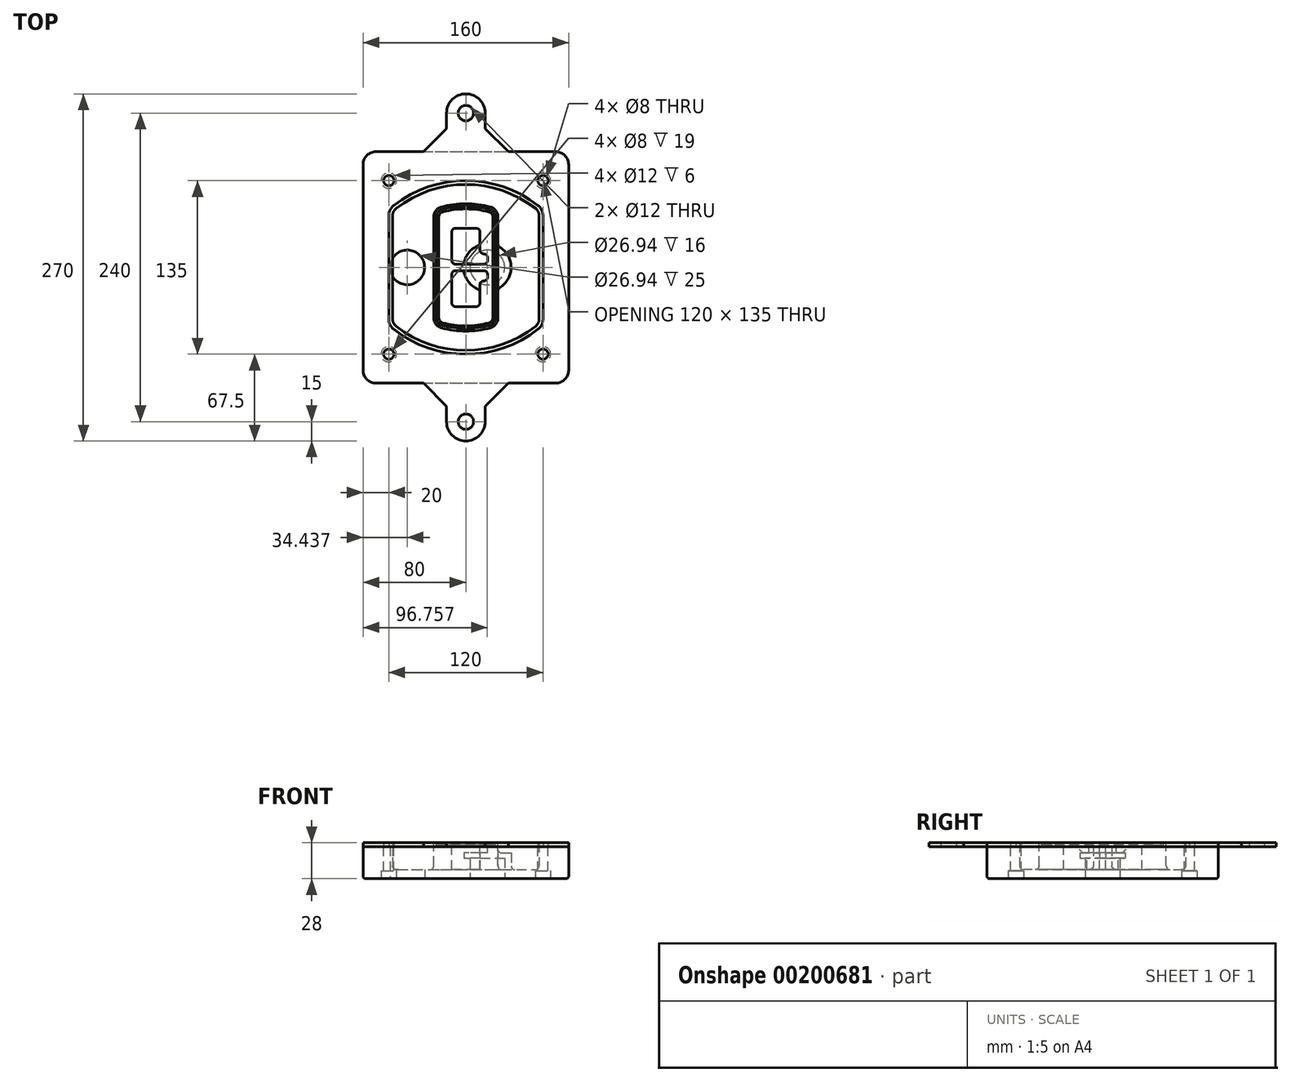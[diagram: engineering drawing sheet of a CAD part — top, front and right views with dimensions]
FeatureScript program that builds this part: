
annotation { "Feature Type Name" : "Feature", "Feature Type Description" : "" }
export const myFeature = defineFeature(function(context is Context, id is Id, definition is map)
    precondition{}
    {
        {
            var Q0;
            Q0=qCreatedBy(makeId("Top.planeOp"),FACE);
            var sketch = newSketch(context, id + "F0", { "sketchPlane" : qUnion([Q0])});
            skPoint(sketch, "E0.rect.middle", {"position": v(0, 0) * mm});
            skLineSegment(sketch, "E1.bottom", {"start": v(-70, -90) * mm, "end": v(70, -90) * mm});
            skLineSegment(sketch, "E1.top", {"start": v(-70, 90) * mm, "end": v(70, 90) * mm});
            skLineSegment(sketch, "E1.left", {"start": v(-80, -80) * mm, "end": v(-80, 80) * mm});
            skLineSegment(sketch, "E1.right", {"start": v(80, -80) * mm, "end": v(80, 80) * mm});
            skLineSegment(sketch, "E2", {"start": v(-80, 90) * mm, "end": v(80, -90) * mm, "construction": true});
            skLineSegment(sketch, "E3", {"start": v(80, 90) * mm, "end": v(-80, -90) * mm, "construction": true});
            skCircle(sketch, "E4", {"center": v(-60, 67.5) * mm, "radius": 4 * mm});
            skCircle(sketch, "E5", {"center": v(60, 67.5) * mm, "radius": 4 * mm});
            skCircle(sketch, "E6", {"center": v(60, -67.5) * mm, "radius": 4 * mm});
            skCircle(sketch, "E7", {"center": v(-60, -67.5) * mm, "radius": 4 * mm});
            skLineSegment(sketch, "E8", {"start": v(-60, 67.5) * mm, "end": v(60, 67.5) * mm, "construction": true});
            skLineSegment(sketch, "E9", {"start": v(60, 67.5) * mm, "end": v(60, -67.5) * mm, "construction": true});
            skLineSegment(sketch, "E10", {"start": v(60, -67.5) * mm, "end": v(-60, -67.5) * mm, "construction": true});
            skLineSegment(sketch, "E11", {"start": v(-60, -67.5) * mm, "end": v(-60, 67.5) * mm, "construction": true});
            skLineSegment(sketch, "E12", {"start": v(-60, 40.3) * mm, "end": v(-60, -40.3) * mm});
            skLineSegment(sketch, "E13", {"start": v(60, 40.3) * mm, "end": v(60, -40.3) * mm});
            skArc(sketch, "E14", {"start": v(56.15, 48.18) * mm, "mid": v(0, 67.5) * mm, "end": v(-56.15, 48.18) * mm});
            skArc(sketch, "E15", {"start": v(-56.15, -48.18) * mm, "mid": v(0, -67.5) * mm, "end": v(56.15, -48.18) * mm});
            skLineSegment(sketch, "E16", {"start": v(-60, 0) * mm, "end": v(60, 0) * mm, "construction": true});
            skPoint(sketch, "E17.visualSharp", {"position": v(-60, -45) * mm});
            skArc(sketch, "E17.filletArc", {"start": v(-60, -40.3) * mm, "mid": v(-58.99, -44.68) * mm, "end": v(-56.15, -48.18) * mm});
            skPoint(sketch, "E18.visualSharp", {"position": v(-60, 45) * mm});
            skArc(sketch, "E18.filletArc", {"start": v(-56.15, 48.18) * mm, "mid": v(-58.99, 44.68) * mm, "end": v(-60, 40.3) * mm});
            skPoint(sketch, "E19.visualSharp", {"position": v(60, 45) * mm});
            skArc(sketch, "E19.filletArc", {"start": v(60, 40.3) * mm, "mid": v(58.99, 44.68) * mm, "end": v(56.15, 48.18) * mm});
            skPoint(sketch, "E20.visualSharp", {"position": v(60, -45) * mm});
            skArc(sketch, "E20.filletArc", {"start": v(56.15, -48.18) * mm, "mid": v(58.99, -44.68) * mm, "end": v(60, -40.3) * mm});
            skPoint(sketch, "E21.visualSharp", {"position": v(-80, 90) * mm});
            skArc(sketch, "E21.filletArc", {"start": v(-70, 90) * mm, "mid": v(-77.07, 87.07) * mm, "end": v(-80, 80) * mm});
            skPoint(sketch, "E22.visualSharp", {"position": v(80, 90) * mm});
            skArc(sketch, "E22.filletArc", {"start": v(80, 80) * mm, "mid": v(77.07, 87.07) * mm, "end": v(70, 90) * mm});
            skPoint(sketch, "E23.visualSharp", {"position": v(80, -90) * mm});
            skArc(sketch, "E23.filletArc", {"start": v(70, -90) * mm, "mid": v(77.07, -87.07) * mm, "end": v(80, -80) * mm});
            skPoint(sketch, "E24.visualSharp", {"position": v(-80, -90) * mm});
            skArc(sketch, "E24.filletArc", {"start": v(-80, -80) * mm, "mid": v(-77.07, -87.07) * mm, "end": v(-70, -90) * mm});
            skArc(sketch, "E25.0", {"start": v(57, 40.3) * mm, "mid": v(56.3, 43.36) * mm, "end": v(54.3, 45.81) * mm});
            skLineSegment(sketch, "E25.1", {"start": v(57, 40.3) * mm, "end": v(57, -40.3) * mm});
            skArc(sketch, "E25.2", {"start": v(54.3, -45.81) * mm, "mid": v(56.3, -43.36) * mm, "end": v(57, -40.3) * mm});
            skArc(sketch, "E25.3", {"start": v(-54.3, -45.81) * mm, "mid": v(0, -64.5) * mm, "end": v(54.3, -45.81) * mm});
            skArc(sketch, "E25.4", {"start": v(-57, -40.3) * mm, "mid": v(-56.3, -43.36) * mm, "end": v(-54.3, -45.81) * mm});
            skArc(sketch, "E25.5", {"start": v(54.3, 45.81) * mm, "mid": v(0, 64.5) * mm, "end": v(-54.3, 45.81) * mm});
            skLineSegment(sketch, "E25.6", {"start": v(-57, 40.3) * mm, "end": v(-57, -40.3) * mm});
            skArc(sketch, "E25.7", {"start": v(-54.3, 45.81) * mm, "mid": v(-56.3, 43.36) * mm, "end": v(-57, 40.3) * mm});
            skArc(sketch, "E26.0", {"start": v(-58.62, 51.33) * mm, "mid": v(-62.58, 46.43) * mm, "end": v(-64, 40.3) * mm});
            skArc(sketch, "E26.1", {"start": v(58.62, 51.33) * mm, "mid": v(0, 71.5) * mm, "end": v(-58.62, 51.33) * mm});
            skArc(sketch, "E26.2", {"start": v(64, 40.3) * mm, "mid": v(62.58, 46.43) * mm, "end": v(58.62, 51.33) * mm});
            skLineSegment(sketch, "E26.3", {"start": v(64, 40.3) * mm, "end": v(64, -40.3) * mm});
            skArc(sketch, "E26.4", {"start": v(58.62, -51.33) * mm, "mid": v(62.58, -46.43) * mm, "end": v(64, -40.3) * mm});
            skLineSegment(sketch, "E26.5", {"start": v(-64, 40.3) * mm, "end": v(-64, -40.3) * mm});
            skArc(sketch, "E26.6", {"start": v(-58.62, -51.33) * mm, "mid": v(0, -71.5) * mm, "end": v(58.62, -51.33) * mm});
            skArc(sketch, "E26.7", {"start": v(-64, -40.3) * mm, "mid": v(-62.58, -46.43) * mm, "end": v(-58.62, -51.33) * mm});
            skSolve(sketch);
        }
        {
            var Q0;
            Q0=makeQuery(id+"F0.imprint","IMPRINT",FACE,{"disambiguationData":[TD([[makeQuery(id+"F0.imprint","IMPRINT",EDGE,{"derivedFrom":sQuery(id+"F0.wireOp",EDGE,"E1.bottom")}),1.0]])]});
            var Q1;
            Q1=makeQuery(id+"F0.imprint","IMPRINT",FACE,{"disambiguationData":[TD([[makeQuery(id+"F0.imprint","IMPRINT",EDGE,{"derivedFrom":sQuery(id+"F0.wireOp",EDGE,"E12")}),1.0]])]});
            var Q2;
            Q2=makeQuery(id+"F0.imprint","IMPRINT",FACE,{"disambiguationData":[TD([[makeQuery(id+"F0.imprint","IMPRINT",EDGE,{"derivedFrom":sQuery(id+"F0.wireOp",EDGE,"E25.0")}),1.0]])]});
            var Q3;
            Q3=makeQuery(id+"F0.imprint","IMPRINT",FACE,{"disambiguationData":[TD([[makeQuery(id+"F0.imprint","IMPRINT",EDGE,{"derivedFrom":sQuery(id+"F0.wireOp",EDGE,"E12")}),-1.0]])]});
            extrude(context, id + "F1", {"entities" : qUnion([Q0, Q1, Q2, Q3]), "oppositeDirection" : true, "depth" : 25 * mm});
        }
        {
            var Q0;
            Q0=makeQuery(id+"F0.imprint","IMPRINT",FACE,{"disambiguationData":[TD([[makeQuery(id+"F0.imprint","IMPRINT",EDGE,{"derivedFrom":sQuery(id+"F0.wireOp",EDGE,"E12")}),1.0]])]});
            extrude(context, id + "F2", {"entities" : qUnion([Q0]), "operationType" : NewBodyOperationType.ADD, "depth" : 3 * mm});
        }
        {
            var Q0;
            Q0=makeQuery(id+"F0.imprint","IMPRINT",FACE,{"disambiguationData":[TD([[makeQuery(id+"F0.imprint","IMPRINT",EDGE,{"derivedFrom":sQuery(id+"F0.wireOp",EDGE,"E25.0")}),1.0]])]});
            extrude(context, id + "F3", {"entities" : qUnion([Q0]), "operationType" : NewBodyOperationType.REMOVE, "oppositeDirection" : true, "depth" : 18 * mm});
        }
        {
            var Q0;
            Q0=makeQuery(id+"F2.opExtrude","CAP_FACE",FACE,{"disambiguationData":[OSD([sQuery(id+"F0.wireOp",EDGE,"E12"),sQuery(id+"F0.wireOp",EDGE,"E13"),sQuery(id+"F0.wireOp",EDGE,"E14"),sQuery(id+"F0.wireOp",EDGE,"E15"),sQuery(id+"F0.wireOp",EDGE,"E17.filletArc"),sQuery(id+"F0.wireOp",EDGE,"E18.filletArc"),sQuery(id+"F0.wireOp",EDGE,"E19.filletArc"),sQuery(id+"F0.wireOp",EDGE,"E20.filletArc"),sQuery(id+"F0.wireOp",EDGE,"E25.0"),sQuery(id+"F0.wireOp",EDGE,"E25.1"),sQuery(id+"F0.wireOp",EDGE,"E25.2"),sQuery(id+"F0.wireOp",EDGE,"E25.3"),sQuery(id+"F0.wireOp",EDGE,"E25.4"),sQuery(id+"F0.wireOp",EDGE,"E25.5"),sQuery(id+"F0.wireOp",EDGE,"E25.6"),sQuery(id+"F0.wireOp",EDGE,"E25.7")])],"isStart":false});
            var sketch = newSketch(context, id + "F4", { "sketchPlane" : qUnion([Q0])});
            skArc(sketch, "E27.0", {"start": v(-19.08, -46.97) * mm, "mid": v(0, -49.5) * mm, "end": v(19.08, -46.97) * mm});
            skArc(sketch, "E28.0", {"start": v(19.08, 46.97) * mm, "mid": v(0, 49.5) * mm, "end": v(-19.08, 46.97) * mm});
            skLineSegment(sketch, "E29", {"start": v(-25, 39.25) * mm, "end": v(-25, -39.25) * mm});
            skLineSegment(sketch, "E30", {"start": v(25, 39.25) * mm, "end": v(25, -39.25) * mm});
            skLineSegment(sketch, "E31", {"start": v(-25, 45.1) * mm, "end": v(25, 45.1) * mm, "construction": true});
            skLineSegment(sketch, "E32", {"start": v(-25, -45.1) * mm, "end": v(25, -45.1) * mm, "construction": true});
            skPoint(sketch, "E33.visualSharp", {"position": v(-25, 45.1) * mm});
            skArc(sketch, "E33.filletArc", {"start": v(-19.08, 46.97) * mm, "mid": v(-23.35, 44.11) * mm, "end": v(-25, 39.25) * mm});
            skPoint(sketch, "E34.visualSharp", {"position": v(25, 45.1) * mm});
            skArc(sketch, "E34.filletArc", {"start": v(25, 39.25) * mm, "mid": v(23.35, 44.11) * mm, "end": v(19.08, 46.97) * mm});
            skPoint(sketch, "E35.visualSharp", {"position": v(25, -45.1) * mm});
            skArc(sketch, "E35.filletArc", {"start": v(19.08, -46.97) * mm, "mid": v(23.35, -44.11) * mm, "end": v(25, -39.25) * mm});
            skPoint(sketch, "E36.visualSharp", {"position": v(-25, -45.1) * mm});
            skArc(sketch, "E36.filletArc", {"start": v(-25, -39.25) * mm, "mid": v(-23.35, -44.11) * mm, "end": v(-19.08, -46.97) * mm});
            skArc(sketch, "E37.0", {"start": v(54.3, 45.81) * mm, "mid": v(0, 64.5) * mm, "end": v(-54.3, 45.81) * mm});
            skArc(sketch, "E37.1", {"start": v(-54.3, 45.81) * mm, "mid": v(-56.3, 43.36) * mm, "end": v(-57, 40.3) * mm});
            skLineSegment(sketch, "E37.2", {"start": v(-57, 40.3) * mm, "end": v(-57, -40.3) * mm});
            skArc(sketch, "E37.3", {"start": v(-57, -40.3) * mm, "mid": v(-56.3, -43.36) * mm, "end": v(-54.3, -45.81) * mm});
            skArc(sketch, "E37.4", {"start": v(-54.3, -45.81) * mm, "mid": v(0, -64.5) * mm, "end": v(54.3, -45.81) * mm});
            skArc(sketch, "E37.5", {"start": v(54.3, -45.81) * mm, "mid": v(56.3, -43.36) * mm, "end": v(57, -40.3) * mm});
            skLineSegment(sketch, "E37.6", {"start": v(57, 40.3) * mm, "end": v(57, -40.3) * mm});
            skArc(sketch, "E37.7", {"start": v(57, 40.3) * mm, "mid": v(56.3, 43.36) * mm, "end": v(54.3, 45.81) * mm});
            skLineSegment(sketch, "E38.0", {"start": v(23, 39.25) * mm, "end": v(23, -39.25) * mm});
            skArc(sketch, "E38.1", {"start": v(18.56, -45.04) * mm, "mid": v(21.76, -42.9) * mm, "end": v(23, -39.25) * mm});
            skArc(sketch, "E38.2", {"start": v(-18.56, -45.04) * mm, "mid": v(0, -47.5) * mm, "end": v(18.56, -45.04) * mm});
            skArc(sketch, "E38.3", {"start": v(-23, -39.25) * mm, "mid": v(-21.76, -42.9) * mm, "end": v(-18.56, -45.04) * mm});
            skLineSegment(sketch, "E38.4", {"start": v(-23, 39.25) * mm, "end": v(-23, -39.25) * mm});
            skArc(sketch, "E38.5", {"start": v(23, 39.25) * mm, "mid": v(21.76, 42.9) * mm, "end": v(18.56, 45.04) * mm});
            skArc(sketch, "E38.6", {"start": v(-18.56, 45.04) * mm, "mid": v(-21.76, 42.9) * mm, "end": v(-23, 39.25) * mm});
            skArc(sketch, "E38.7", {"start": v(18.56, 45.04) * mm, "mid": v(0, 47.5) * mm, "end": v(-18.56, 45.04) * mm});
            skArc(sketch, "E39.0", {"start": v(21, 39.25) * mm, "mid": v(20.18, 41.68) * mm, "end": v(18.04, 43.1) * mm});
            skLineSegment(sketch, "E39.1", {"start": v(21, 39.25) * mm, "end": v(21, -39.25) * mm});
            skArc(sketch, "E39.2", {"start": v(18.04, -43.1) * mm, "mid": v(20.18, -41.68) * mm, "end": v(21, -39.25) * mm});
            skArc(sketch, "E39.3", {"start": v(-18.04, -43.1) * mm, "mid": v(0, -45.5) * mm, "end": v(18.04, -43.1) * mm});
            skArc(sketch, "E39.4", {"start": v(-21, -39.25) * mm, "mid": v(-20.18, -41.68) * mm, "end": v(-18.04, -43.1) * mm});
            skArc(sketch, "E39.5", {"start": v(18.04, 43.1) * mm, "mid": v(0, 45.5) * mm, "end": v(-18.04, 43.1) * mm});
            skLineSegment(sketch, "E39.6", {"start": v(-21, 39.25) * mm, "end": v(-21, -39.25) * mm});
            skArc(sketch, "E39.7", {"start": v(-18.04, 43.1) * mm, "mid": v(-20.18, 41.68) * mm, "end": v(-21, 39.25) * mm});
            skLineSegment(sketch, "E40", {"start": v(-25, 0) * mm, "end": v(25, 0) * mm, "construction": true});
            skLineSegment(sketch, "E41", {"start": v(-11, 5.5) * mm, "end": v(-11, 27.5) * mm});
            skLineSegment(sketch, "E42", {"start": v(-8, 30.5) * mm, "end": v(8, 30.5) * mm});
            skLineSegment(sketch, "E43", {"start": v(11, 27.5) * mm, "end": v(11, 13.5) * mm});
            skLineSegment(sketch, "E44", {"start": v(14, 10.5) * mm, "end": v(14, 10.5) * mm});
            skLineSegment(sketch, "E45", {"start": v(17, 7.5) * mm, "end": v(17, 5.5) * mm});
            skLineSegment(sketch, "E46", {"start": v(14, 2.5) * mm, "end": v(-8, 2.5) * mm});
            skPoint(sketch, "E47.visualSharp", {"position": v(-11, 30.5) * mm});
            skArc(sketch, "E47.filletArc", {"start": v(-8, 30.5) * mm, "mid": v(-10.12, 29.62) * mm, "end": v(-11, 27.5) * mm});
            skPoint(sketch, "E48.visualSharp", {"position": v(11, 30.5) * mm});
            skArc(sketch, "E48.filletArc", {"start": v(11, 27.5) * mm, "mid": v(10.12, 29.62) * mm, "end": v(8, 30.5) * mm});
            skPoint(sketch, "E49.visualSharp", {"position": v(11, 10.5) * mm});
            skArc(sketch, "E49.filletArc", {"start": v(11, 13.5) * mm, "mid": v(11.88, 11.38) * mm, "end": v(14, 10.5) * mm});
            skPoint(sketch, "E50.visualSharp", {"position": v(17, 10.5) * mm});
            skArc(sketch, "E50.filletArc", {"start": v(17, 7.5) * mm, "mid": v(16.12, 9.62) * mm, "end": v(14, 10.5) * mm});
            skPoint(sketch, "E51.visualSharp", {"position": v(17, 2.5) * mm});
            skArc(sketch, "E51.filletArc", {"start": v(14, 2.5) * mm, "mid": v(16.12, 3.38) * mm, "end": v(17, 5.5) * mm});
            skPoint(sketch, "E52.visualSharp", {"position": v(-11, 2.5) * mm});
            skArc(sketch, "E52.filletArc", {"start": v(-11, 5.5) * mm, "mid": v(-10.12, 3.38) * mm, "end": v(-8, 2.5) * mm});
            skLineSegment(sketch, "E53.0.MirrorCS", {"start": v(14, -2.5) * mm, "end": v(-8, -2.5) * mm});
            skArc(sketch, "E54.0.MirrorCS", {"start": v(-11, -5.5) * mm, "mid": v(-10.12, -3.38) * mm, "end": v(-8, -2.5) * mm});
            skLineSegment(sketch, "E55.0.MirrorCS", {"start": v(-11, -5.5) * mm, "end": v(-11, -27.5) * mm});
            skArc(sketch, "E56.0.MirrorCS", {"start": v(-8, -30.5) * mm, "mid": v(-10.12, -29.62) * mm, "end": v(-11, -27.5) * mm});
            skLineSegment(sketch, "E57.0.MirrorCS", {"start": v(-8, -30.5) * mm, "end": v(8, -30.5) * mm});
            skArc(sketch, "E58.0.MirrorCS", {"start": v(11, -27.5) * mm, "mid": v(10.12, -29.62) * mm, "end": v(8, -30.5) * mm});
            skLineSegment(sketch, "E59.0.MirrorCS", {"start": v(11, -27.5) * mm, "end": v(11, -13.5) * mm});
            skArc(sketch, "E60.0.MirrorCS", {"start": v(11, -13.5) * mm, "mid": v(11.88, -11.38) * mm, "end": v(14, -10.5) * mm});
            skArc(sketch, "E61.0.MirrorCS", {"start": v(17, -7.5) * mm, "mid": v(16.12, -9.62) * mm, "end": v(14, -10.5) * mm});
            skLineSegment(sketch, "E62.0.MirrorCS", {"start": v(17, -7.5) * mm, "end": v(17, -5.5) * mm});
            skArc(sketch, "E63.0.MirrorCS", {"start": v(14, -2.5) * mm, "mid": v(16.12, -3.38) * mm, "end": v(17, -5.5) * mm});
            skSolve(sketch);
        }
        {
            var Q0;
            Q0=makeQuery(id+"F4.imprint","IMPRINT",FACE,{"disambiguationData":[TD([[makeQuery(id+"F4.imprint","IMPRINT",EDGE,{"derivedFrom":sQuery(id+"F4.wireOp",EDGE,"E27.0")}),1.0]])]});
            var Q1;
            Q1=makeQuery(id+"F4.imprint","IMPRINT",FACE,{"disambiguationData":[TD([[makeQuery(id+"F4.imprint","IMPRINT",EDGE,{"derivedFrom":sQuery(id+"F4.wireOp",EDGE,"E38.0")}),-1.0]])]});
            var Q2;
            Q2=makeQuery(id+"F4.imprint","IMPRINT",FACE,{"disambiguationData":[TD([[makeQuery(id+"F4.imprint","IMPRINT",EDGE,{"derivedFrom":sQuery(id+"F4.wireOp",EDGE,"E39.0")}),1.0]])]});
            extrude(context, id + "F5", {"entities" : qUnion([Q0, Q1, Q2]), "operationType" : NewBodyOperationType.ADD, "endBound" : BoundingType.UP_TO_NEXT, "oppositeDirection" : true, "depth" : 25 * mm});
        }
        {
            var Q0;
            Q0=makeQuery(id+"F4.imprint","IMPRINT",FACE,{"disambiguationData":[TD([[makeQuery(id+"F4.imprint","IMPRINT",EDGE,{"derivedFrom":sQuery(id+"F4.wireOp",EDGE,"E38.0")}),-1.0]])]});
            extrude(context, id + "F6", {"entities" : qUnion([Q0]), "operationType" : NewBodyOperationType.REMOVE, "oppositeDirection" : true, "depth" : 2 * mm});
        }
        {
            var Q0;
            Q0=makeQuery(id+"F1.opExtrude","CAP_FACE",FACE,{"disambiguationData":[OSD([sQuery(id+"F0.wireOp",EDGE,"E1.bottom"),sQuery(id+"F0.wireOp",EDGE,"E1.top"),sQuery(id+"F0.wireOp",EDGE,"E1.left"),sQuery(id+"F0.wireOp",EDGE,"E1.right"),sQuery(id+"F0.wireOp",EDGE,"E4"),sQuery(id+"F0.wireOp",EDGE,"E5"),sQuery(id+"F0.wireOp",EDGE,"E6"),sQuery(id+"F0.wireOp",EDGE,"E7"),sQuery(id+"F0.wireOp",EDGE,"E21.filletArc"),sQuery(id+"F0.wireOp",EDGE,"E22.filletArc"),sQuery(id+"F0.wireOp",EDGE,"E23.filletArc"),sQuery(id+"F0.wireOp",EDGE,"E24.filletArc")])],"isStart":false});
            var sketch = newSketch(context, id + "F7", { "sketchPlane" : qUnion([Q0])});
            skCircle(sketch, "E64", {"center": v(16.76, 0) * mm, "radius": 13.47 * mm});
            skCircle(sketch, "E65", {"center": v(-45.56, 0) * mm, "radius": 13.47 * mm});
            skLineSegment(sketch, "E66", {"start": v(80, 0) * mm, "end": v(-80, 0) * mm});
            skCircle(sketch, "E67", {"center": v(16.76, 0) * mm, "radius": 18.47 * mm});
            skCircle(sketch, "E68", {"center": v(60, -67.5) * mm, "radius": 6 * mm});
            skCircle(sketch, "E69", {"center": v(-60, -67.5) * mm, "radius": 6 * mm});
            skCircle(sketch, "E70", {"center": v(-60, 67.5) * mm, "radius": 6 * mm});
            skCircle(sketch, "E71", {"center": v(60, 67.5) * mm, "radius": 6 * mm});
            skSolve(sketch);
        }
        {
            var Q0;
            {var subQ1=sQuery(id+"F7.wireOp",EDGE,"E66");var subQ4=sQuery(id+"F7.wireOp",EDGE,"E64");var subQ6=makeQuery(id+"F7.imprint","INTERSECT",VERTEX,{"disambiguationData":[OD(0.0)],"derivedFrom":[subQ4,subQ1]});Q0=makeQuery(id+"F7.imprint","IMPRINT",FACE,{"disambiguationData":[TD([[makeQuery(id+"F7.imprint","IMPRINT",EDGE,{"disambiguationData":[TD([[subQ6,-1.0]])],"derivedFrom":subQ4}),-1.0]])]});}
            var Q1;
            {var subQ0=sQuery(id+"F7.wireOp",EDGE,"E66");var subQ1=sQuery(id+"F7.wireOp",EDGE,"E64");var subQ3=makeQuery(id+"F7.imprint","INTERSECT",VERTEX,{"disambiguationData":[OD(0.0)],"derivedFrom":[subQ1,subQ0]});Q1=makeQuery(id+"F7.imprint","IMPRINT",FACE,{"disambiguationData":[TD([[makeQuery(id+"F7.imprint","IMPRINT",EDGE,{"disambiguationData":[TD([[subQ3,-1.0]])],"derivedFrom":subQ1}),1.0]])]});}
            var Q2;
            {var subQ0=sQuery(id+"F7.wireOp",EDGE,"E66");var subQ1=sQuery(id+"F7.wireOp",EDGE,"E64");var subQ3=makeQuery(id+"F7.imprint","INTERSECT",VERTEX,{"disambiguationData":[OD(0.0)],"derivedFrom":[subQ1,subQ0]});Q2=makeQuery(id+"F7.imprint","IMPRINT",FACE,{"disambiguationData":[TD([[makeQuery(id+"F7.imprint","IMPRINT",EDGE,{"disambiguationData":[TD([[subQ3,1.0]])],"derivedFrom":subQ1}),1.0]])]});}
            var Q3;
            {var subQ1=sQuery(id+"F7.wireOp",EDGE,"E66");var subQ4=sQuery(id+"F7.wireOp",EDGE,"E64");var subQ6=makeQuery(id+"F7.imprint","INTERSECT",VERTEX,{"disambiguationData":[OD(0.0)],"derivedFrom":[subQ4,subQ1]});Q3=makeQuery(id+"F7.imprint","IMPRINT",FACE,{"disambiguationData":[TD([[makeQuery(id+"F7.imprint","IMPRINT",EDGE,{"disambiguationData":[TD([[subQ6,1.0]])],"derivedFrom":subQ4}),-1.0]])]});}
            extrude(context, id + "F8", {"entities" : qUnion([Q0, Q1, Q2, Q3]), "operationType" : NewBodyOperationType.ADD, "oppositeDirection" : true, "depth" : 20 * mm});
        }
        {
            var Q0;
            {var subQ0=sQuery(id+"F7.wireOp",EDGE,"E66");var subQ1=sQuery(id+"F7.wireOp",EDGE,"E64");var subQ3=makeQuery(id+"F7.imprint","INTERSECT",VERTEX,{"disambiguationData":[OD(0.0)],"derivedFrom":[subQ1,subQ0]});Q0=makeQuery(id+"F7.imprint","IMPRINT",FACE,{"disambiguationData":[TD([[makeQuery(id+"F7.imprint","IMPRINT",EDGE,{"disambiguationData":[TD([[subQ3,-1.0]])],"derivedFrom":subQ1}),1.0]])]});}
            var Q1;
            {var subQ0=sQuery(id+"F7.wireOp",EDGE,"E66");var subQ1=sQuery(id+"F7.wireOp",EDGE,"E64");var subQ3=makeQuery(id+"F7.imprint","INTERSECT",VERTEX,{"disambiguationData":[OD(0.0)],"derivedFrom":[subQ1,subQ0]});Q1=makeQuery(id+"F7.imprint","IMPRINT",FACE,{"disambiguationData":[TD([[makeQuery(id+"F7.imprint","IMPRINT",EDGE,{"disambiguationData":[TD([[subQ3,1.0]])],"derivedFrom":subQ1}),1.0]])]});}
            extrude(context, id + "F9", {"entities" : qUnion([Q0, Q1]), "operationType" : NewBodyOperationType.REMOVE, "oppositeDirection" : true, "depth" : 16 * mm});
        }
        {
            var Q0;
            {var subQ0=sQuery(id+"F7.wireOp",EDGE,"E66");var subQ1=sQuery(id+"F7.wireOp",EDGE,"E65");var subQ3=makeQuery(id+"F7.imprint","INTERSECT",VERTEX,{"disambiguationData":[OD(0.0)],"derivedFrom":[subQ1,subQ0]});Q0=makeQuery(id+"F7.imprint","IMPRINT",FACE,{"disambiguationData":[TD([[makeQuery(id+"F7.imprint","IMPRINT",EDGE,{"disambiguationData":[TD([[subQ3,-1.0]])],"derivedFrom":subQ1}),1.0]])]});}
            var Q1;
            {var subQ0=sQuery(id+"F7.wireOp",EDGE,"E66");var subQ1=sQuery(id+"F7.wireOp",EDGE,"E65");var subQ3=makeQuery(id+"F7.imprint","INTERSECT",VERTEX,{"disambiguationData":[OD(0.0)],"derivedFrom":[subQ1,subQ0]});Q1=makeQuery(id+"F7.imprint","IMPRINT",FACE,{"disambiguationData":[TD([[makeQuery(id+"F7.imprint","IMPRINT",EDGE,{"disambiguationData":[TD([[subQ3,1.0]])],"derivedFrom":subQ1}),1.0]])]});}
            extrude(context, id + "F10", {"entities" : qUnion([Q0, Q1]), "operationType" : NewBodyOperationType.REMOVE, "oppositeDirection" : true, "depth" : 25 * mm});
        }
        {
            var Q0;
            Q0=makeQuery(id+"F7.imprint","IMPRINT",FACE,{"disambiguationData":[TD([[makeQuery(id+"F7.imprint","IMPRINT",EDGE,{"derivedFrom":sQuery(id+"F7.wireOp",EDGE,"E68")}),1.0]])]});
            var Q1;
            Q1=makeQuery(id+"F7.imprint","IMPRINT",FACE,{"disambiguationData":[TD([[makeQuery(id+"F7.imprint","IMPRINT",EDGE,{"derivedFrom":makeQuery(id+"F1.opExtrude","CAP_EDGE",EDGE,{"disambiguationData":[OSD([sQuery(id+"F0.wireOp",EDGE,"E5")])],"isStart":false})}),-1.0]])]});
            var Q2;
            Q2=makeQuery(id+"F7.imprint","IMPRINT",FACE,{"disambiguationData":[TD([[makeQuery(id+"F7.imprint","IMPRINT",EDGE,{"derivedFrom":sQuery(id+"F7.wireOp",EDGE,"E69")}),1.0]])]});
            var Q3;
            Q3=makeQuery(id+"F7.imprint","IMPRINT",FACE,{"disambiguationData":[TD([[makeQuery(id+"F7.imprint","IMPRINT",EDGE,{"derivedFrom":makeQuery(id+"F1.opExtrude","CAP_EDGE",EDGE,{"disambiguationData":[OSD([sQuery(id+"F0.wireOp",EDGE,"E4")])],"isStart":false})}),-1.0]])]});
            var Q4;
            Q4=makeQuery(id+"F7.imprint","IMPRINT",FACE,{"disambiguationData":[TD([[makeQuery(id+"F7.imprint","IMPRINT",EDGE,{"derivedFrom":sQuery(id+"F7.wireOp",EDGE,"E70")}),1.0]])]});
            var Q5;
            Q5=makeQuery(id+"F7.imprint","IMPRINT",FACE,{"disambiguationData":[TD([[makeQuery(id+"F7.imprint","IMPRINT",EDGE,{"derivedFrom":makeQuery(id+"F1.opExtrude","CAP_EDGE",EDGE,{"disambiguationData":[OSD([sQuery(id+"F0.wireOp",EDGE,"E7")])],"isStart":false})}),-1.0]])]});
            var Q6;
            Q6=makeQuery(id+"F7.imprint","IMPRINT",FACE,{"disambiguationData":[TD([[makeQuery(id+"F7.imprint","IMPRINT",EDGE,{"derivedFrom":sQuery(id+"F7.wireOp",EDGE,"E71")}),1.0]])]});
            var Q7;
            Q7=makeQuery(id+"F7.imprint","IMPRINT",FACE,{"disambiguationData":[TD([[makeQuery(id+"F7.imprint","IMPRINT",EDGE,{"derivedFrom":makeQuery(id+"F1.opExtrude","CAP_EDGE",EDGE,{"disambiguationData":[OSD([sQuery(id+"F0.wireOp",EDGE,"E6")])],"isStart":false})}),-1.0]])]});
            extrude(context, id + "F11", {"entities" : qUnion([Q0, Q1, Q2, Q3, Q4, Q5, Q6, Q7]), "operationType" : NewBodyOperationType.REMOVE, "oppositeDirection" : true, "depth" : 6 * mm});
        }
        {
            var Q0;
            Q0=makeQuery(id+"F9.boolean.opBoolean","COPY",FACE,{"derivedFrom":makeQuery(id+"F9.opExtrude","CAP_FACE",FACE,{"disambiguationData":[OSD([sQuery(id+"F7.wireOp",EDGE,"E64")])],"isStart":false})});
            var sketch = newSketch(context, id + "F12", { "sketchPlane" : qUnion([Q0])});
            skArc(sketch, "E72.0", {"start": v(11, 17.55) * mm, "mid": v(2.57, 11.82) * mm, "end": v(-1.54, 2.5) * mm});
            skArc(sketch, "E72.1", {"start": v(-1.54, -2.5) * mm, "mid": v(2.57, -11.82) * mm, "end": v(11, -17.55) * mm});
            skLineSegment(sketch, "E73", {"start": v(-1.54, -2.5) * mm, "end": v(14, -2.5) * mm});
            skLineSegment(sketch, "E74.0", {"start": v(14, 2.5) * mm, "end": v(-1.54, 2.5) * mm});
            skArc(sketch, "E74.1", {"start": v(14, 2.5) * mm, "mid": v(16.12, 3.38) * mm, "end": v(17, 5.5) * mm});
            skLineSegment(sketch, "E74.2", {"start": v(17, 7.5) * mm, "end": v(17, 5.5) * mm});
            skArc(sketch, "E74.3", {"start": v(17, 7.5) * mm, "mid": v(16.12, 9.62) * mm, "end": v(14, 10.5) * mm});
            skArc(sketch, "E74.4", {"start": v(11, 13.5) * mm, "mid": v(11.88, 11.38) * mm, "end": v(14, 10.5) * mm});
            skLineSegment(sketch, "E74.5", {"start": v(11, 17.55) * mm, "end": v(11, 13.5) * mm});
            skLineSegment(sketch, "E74.7", {"start": v(14, -2.5) * mm, "end": v(-1.54, -2.5) * mm});
            skArc(sketch, "E74.8", {"start": v(14, -2.5) * mm, "mid": v(16.12, -3.38) * mm, "end": v(17, -5.5) * mm});
            skLineSegment(sketch, "E74.9", {"start": v(17, -7.5) * mm, "end": v(17, -5.5) * mm});
            skArc(sketch, "E74.10", {"start": v(17, -7.5) * mm, "mid": v(16.12, -9.62) * mm, "end": v(14, -10.5) * mm});
            skArc(sketch, "E74.11", {"start": v(11, -13.5) * mm, "mid": v(11.88, -11.38) * mm, "end": v(14, -10.5) * mm});
            skLineSegment(sketch, "E74.12", {"start": v(11, -17.55) * mm, "end": v(11, -13.5) * mm});
            skPoint(sketch, "E75.orphan", {"position": v(11, -27.5) * mm});
            skPoint(sketch, "E76.orphan", {"position": v(-8, -2.5) * mm});
            skPoint(sketch, "E77.orphan", {"position": v(-8, 2.5) * mm});
            skPoint(sketch, "E78.orphan", {"position": v(11, 27.5) * mm});
            skSolve(sketch);
        }
        {
            var Q0;
            {var subQ7=sQuery(id+"F12.wireOp",EDGE,"E72.0");var subQ14=sQuery(id+"F12.wireOp",EDGE,"E72.1");var subQ16=sQuery(id+"F12.wireOp",EDGE,"E74.1");var subQ18=sQuery(id+"F12.wireOp",EDGE,"E74.8");Q0=qUnion([makeQuery(id+"F12.imprint","IMPRINT",FACE,{"disambiguationData":[TD([[makeQuery(id+"F12.imprint","IMPRINT",EDGE,{"derivedFrom":subQ7}),1.0]])]}),makeQuery(id+"F12.imprint","IMPRINT",FACE,{"disambiguationData":[TD([[makeQuery(id+"F12.imprint","IMPRINT",EDGE,{"derivedFrom":subQ14}),1.0]])]}),makeQuery(id+"F12.imprint","IMPRINT",FACE,{"disambiguationData":[TD([[makeQuery(id+"F12.imprint","IMPRINT",EDGE,{"derivedFrom":subQ16}),1.0]])]}),makeQuery(id+"F12.imprint","IMPRINT",FACE,{"disambiguationData":[TD([[makeQuery(id+"F12.imprint","IMPRINT",EDGE,{"derivedFrom":subQ18}),-1.0]])]})]);}
            var Q1;
            Q1=makeQuery(id+"F5.boolean.opBoolean","SPLIT",FACE,{"disambiguationData":[TD([makeQuery(id+"F5.opExtrude","SWEPT_FACE",FACE,{"disambiguationData":[OSD([sQuery(id+"F4.wireOp",EDGE,"E41")])]})])],"derivedFrom":makeQuery(id+"F3.boolean.opBoolean","COPY",FACE,{"derivedFrom":makeQuery(id+"F3.opExtrude","CAP_FACE",FACE,{"disambiguationData":[OSD([sQuery(id+"F0.wireOp",EDGE,"E25.0"),sQuery(id+"F0.wireOp",EDGE,"E25.1"),sQuery(id+"F0.wireOp",EDGE,"E25.2"),sQuery(id+"F0.wireOp",EDGE,"E25.3"),sQuery(id+"F0.wireOp",EDGE,"E25.4"),sQuery(id+"F0.wireOp",EDGE,"E25.5"),sQuery(id+"F0.wireOp",EDGE,"E25.6"),sQuery(id+"F0.wireOp",EDGE,"E25.7")])],"isStart":false})})});
            extrude(context, id + "F13", {"entities" : qUnion([Q0]), "operationType" : NewBodyOperationType.REMOVE, "endBound" : BoundingType.UP_TO_SURFACE, "endBoundEntityFace" : qUnion([Q1]), "depth" : 25 * mm});
        }
        {
            var Q0;
            Q0=makeQuery(id+"F3.boolean.opBoolean","COPY",EDGE,{"derivedFrom":makeQuery(id+"F3.opExtrude","CAP_EDGE",EDGE,{"disambiguationData":[OSD([sQuery(id+"F0.wireOp",EDGE,"E25.6")])],"isStart":false})});
            var Q1;
            Q1=makeQuery(id+"F8.boolean.opBoolean","INTERSECT",EDGE,{"derivedFrom":[makeQuery(id+"F5.opExtrude","SWEPT_FACE",FACE,{"disambiguationData":[OSD([sQuery(id+"F4.wireOp",EDGE,"E30")])]}),makeQuery(id+"F8.opExtrude","CAP_FACE",FACE,{"disambiguationData":[OSD([sQuery(id+"F7.wireOp",EDGE,"E67")])],"isStart":false})]});
            var Q2;
            Q2=makeQuery(id+"F8.boolean.opBoolean","INTERSECT",EDGE,{"disambiguationData":[OD(1.0)],"derivedFrom":[makeQuery(id+"F5.opExtrude","SWEPT_FACE",FACE,{"disambiguationData":[OSD([sQuery(id+"F4.wireOp",EDGE,"E30")])]}),makeQuery(id+"F8.opExtrude","SWEPT_FACE",FACE,{"disambiguationData":[OSD([sQuery(id+"F7.wireOp",EDGE,"E67")])]})]});
            var Q3;
            {var subQ0=sQuery(id+"F4.wireOp",EDGE,"E30");Q3=makeQuery(id+"F8.boolean.opBoolean","SPLIT",EDGE,{"disambiguationData":[TD([makeQuery(id+"F5.opExtrude","SWEPT_FACE",FACE,{"disambiguationData":[OSD([sQuery(id+"F4.wireOp",EDGE,"E35.filletArc")])]})])],"derivedFrom":makeQuery(id+"F5.opExtrude","CAP_EDGE",EDGE,{"disambiguationData":[OSD([subQ0])],"isStart":false})});}
            var Q4;
            {var subQ0=sQuery(id+"F0.wireOp",EDGE,"E25.7");var subQ1=sQuery(id+"F0.wireOp",EDGE,"E25.1");var subQ2=sQuery(id+"F0.wireOp",EDGE,"E25.6");var subQ3=sQuery(id+"F0.wireOp",EDGE,"E25.5");var subQ4=sQuery(id+"F0.wireOp",EDGE,"E25.4");var subQ5=sQuery(id+"F0.wireOp",EDGE,"E25.0");var subQ6=sQuery(id+"F0.wireOp",EDGE,"E25.2");var subQ7=sQuery(id+"F0.wireOp",EDGE,"E25.3");Q4=makeQuery(id+"F8.boolean.opBoolean","INTERSECT",EDGE,{"derivedFrom":[makeQuery(id+"F5.boolean.opBoolean","SPLIT",FACE,{"disambiguationData":[TD([makeQuery(id+"F2.opExtrude","SWEPT_FACE",FACE,{"disambiguationData":[OSD([subQ5])]})])],"derivedFrom":makeQuery(id+"F3.boolean.opBoolean","COPY",FACE,{"derivedFrom":makeQuery(id+"F3.opExtrude","CAP_FACE",FACE,{"disambiguationData":[OSD([subQ5,subQ1,subQ6,subQ7,subQ4,subQ3,subQ2,subQ0])],"isStart":false})})}),makeQuery(id+"F8.opExtrude","SWEPT_FACE",FACE,{"disambiguationData":[OSD([sQuery(id+"F7.wireOp",EDGE,"E67")])]})]});}
            var Q5;
            Q5=makeQuery(id+"F8.boolean.opBoolean","INTERSECT",EDGE,{"disambiguationData":[OD(0.0)],"derivedFrom":[makeQuery(id+"F5.opExtrude","SWEPT_FACE",FACE,{"disambiguationData":[OSD([sQuery(id+"F4.wireOp",EDGE,"E30")])]}),makeQuery(id+"F8.opExtrude","SWEPT_FACE",FACE,{"disambiguationData":[OSD([sQuery(id+"F7.wireOp",EDGE,"E67")])]})]});
            fillet(context, id + "F14", {"entities" : qUnion([Q0, Q1, Q2, Q3, Q4, Q5]), "radius" : 3 * mm, "tangentPropagation" : true, "allowEdgeOverflow" : false});
        }
        {
            var Q0;
            Q0=makeQuery(id+"F1.opExtrude","CAP_EDGE",EDGE,{"disambiguationData":[OSD([sQuery(id+"F0.wireOp",EDGE,"E1.bottom")])],"isStart":false});
            fillet(context, id + "F15", {"entities" : qUnion([Q0]), "radius" : 2 * mm, "tangentPropagation" : true, "allowEdgeOverflow" : false});
        }
        {
            var Q0;
            {var subQ0=sQuery(id+"F0.wireOp",EDGE,"E22.filletArc");var subQ1=sQuery(id+"F0.wireOp",EDGE,"E7");var subQ2=sQuery(id+"F0.wireOp",EDGE,"E6");var subQ3=sQuery(id+"F0.wireOp",EDGE,"E5");var subQ4=sQuery(id+"F0.wireOp",EDGE,"E4");var subQ5=sQuery(id+"F0.wireOp",EDGE,"E1.bottom");var subQ6=sQuery(id+"F0.wireOp",EDGE,"E21.filletArc");var subQ7=sQuery(id+"F0.wireOp",EDGE,"E1.top");var subQ8=sQuery(id+"F0.wireOp",EDGE,"E1.left");var subQ9=sQuery(id+"F0.wireOp",EDGE,"E1.right");var subQ10=sQuery(id+"F0.wireOp",EDGE,"E23.filletArc");var subQ11=sQuery(id+"F0.wireOp",EDGE,"E24.filletArc");Q0=makeQuery(id+"F2.boolean.opBoolean","SPLIT",FACE,{"disambiguationData":[TD([makeQuery(id+"F1.opExtrude","SWEPT_FACE",FACE,{"disambiguationData":[OSD([subQ5])]})])],"derivedFrom":makeQuery(id+"F1.opExtrude","CAP_FACE",FACE,{"disambiguationData":[OSD([subQ5,subQ7,subQ8,subQ9,subQ4,subQ3,subQ2,subQ1,subQ6,subQ0,subQ10,subQ11])],"isStart":true})});}
            var sketch = newSketch(context, id + "F16", { "sketchPlane" : qUnion([Q0])});
            skArc(sketch, "E79.0", {"start": v(56.15, 48.18) * mm, "mid": v(0, 67.5) * mm, "end": v(-56.15, 48.18) * mm});
            skArc(sketch, "E80.0", {"start": v(60, 40.3) * mm, "mid": v(58.99, 44.68) * mm, "end": v(56.15, 48.18) * mm});
            skLineSegment(sketch, "E81.0", {"start": v(60, 40.3) * mm, "end": v(60, -40.3) * mm});
            skArc(sketch, "E82.0", {"start": v(56.15, -48.18) * mm, "mid": v(58.99, -44.68) * mm, "end": v(60, -40.3) * mm});
            skArc(sketch, "E83.0", {"start": v(-56.15, -48.18) * mm, "mid": v(0, -67.5) * mm, "end": v(56.15, -48.18) * mm});
            skArc(sketch, "E84.0", {"start": v(-60, -40.3) * mm, "mid": v(-58.99, -44.68) * mm, "end": v(-56.15, -48.18) * mm});
            skLineSegment(sketch, "E85.0", {"start": v(-60, 40.3) * mm, "end": v(-60, -40.3) * mm});
            skArc(sketch, "E86.0", {"start": v(-56.15, 48.18) * mm, "mid": v(-58.99, 44.68) * mm, "end": v(-60, 40.3) * mm});
            skCircle(sketch, "E87.0", {"center": v(-60, 67.5) * mm, "radius": 4 * mm});
            skCircle(sketch, "E88.0", {"center": v(60, 67.5) * mm, "radius": 4 * mm});
            skCircle(sketch, "E89.0", {"center": v(60, -67.5) * mm, "radius": 4 * mm});
            skCircle(sketch, "E90.0", {"center": v(-60, -67.5) * mm, "radius": 4 * mm});
            skLineSegment(sketch, "E91.0", {"start": v(-80, -80) * mm, "end": v(-80, 80) * mm});
            skArc(sketch, "E92.0", {"start": v(-70, 90) * mm, "mid": v(-77.07, 87.07) * mm, "end": v(-80, 80) * mm});
            skLineSegment(sketch, "E93.0", {"start": v(-70, 90) * mm, "end": v(70, 90) * mm});
            skArc(sketch, "E94.0", {"start": v(80, 80) * mm, "mid": v(77.07, 87.07) * mm, "end": v(70, 90) * mm});
            skLineSegment(sketch, "E95.0", {"start": v(80, -80) * mm, "end": v(80, 80) * mm});
            skArc(sketch, "E96.0", {"start": v(70, -90) * mm, "mid": v(77.07, -87.07) * mm, "end": v(80, -80) * mm});
            skLineSegment(sketch, "E97.0", {"start": v(-70, -90) * mm, "end": v(70, -90) * mm});
            skArc(sketch, "E98.0", {"start": v(-80, -80) * mm, "mid": v(-77.07, -87.07) * mm, "end": v(-70, -90) * mm});
            skLineSegment(sketch, "E99", {"start": v(0, 90) * mm, "end": v(0, 120) * mm, "construction": true});
            skCircle(sketch, "E100", {"center": v(0, 120) * mm, "radius": 6 * mm});
            skArc(sketch, "E101", {"start": v(-15, 120) * mm, "mid": v(0, 135) * mm, "end": v(15, 120) * mm});
            skLineSegment(sketch, "E102", {"start": v(-15, 120) * mm, "end": v(-15, 108) * mm});
            skLineSegment(sketch, "E103", {"start": v(15, 120) * mm, "end": v(15, 108) * mm});
            skLineSegment(sketch, "E104", {"start": v(33, 90) * mm, "end": v(15, 108) * mm});
            skLineSegment(sketch, "E105", {"start": v(-15, 108) * mm, "end": v(-33, 90) * mm});
            skLineSegment(sketch, "E106", {"start": v(-80, 0) * mm, "end": v(80, 0) * mm, "construction": true});
            skLineSegment(sketch, "E107.MirrorCS", {"start": v(0, -90) * mm, "end": v(0, -120) * mm, "construction": true});
            skLineSegment(sketch, "E108.MirrorCS", {"start": v(15, -120) * mm, "end": v(15, -108) * mm});
            skArc(sketch, "E109.MirrorCS", {"start": v(-15, -120) * mm, "mid": v(0, -135) * mm, "end": v(15, -120) * mm});
            skLineSegment(sketch, "E110.MirrorCS", {"start": v(-15, -108) * mm, "end": v(-33, -90) * mm});
            skCircle(sketch, "E111.MirrorC", {"center": v(0, -120) * mm, "radius": 6 * mm});
            skLineSegment(sketch, "E112.MirrorCS", {"start": v(-15, -120) * mm, "end": v(-15, -108) * mm});
            skLineSegment(sketch, "E113.MirrorCS", {"start": v(33, -90) * mm, "end": v(15, -108) * mm});
            skSolve(sketch);
        }
        {
            var Q0;
            Q0 = qSketchRegion(id + "F16", true);
            var Q1;
            Q1=makeQuery(id+"F2.opExtrude","CAP_FACE",FACE,{"disambiguationData":[OSD([sQuery(id+"F0.wireOp",EDGE,"E12"),sQuery(id+"F0.wireOp",EDGE,"E13"),sQuery(id+"F0.wireOp",EDGE,"E14"),sQuery(id+"F0.wireOp",EDGE,"E15"),sQuery(id+"F0.wireOp",EDGE,"E17.filletArc"),sQuery(id+"F0.wireOp",EDGE,"E18.filletArc"),sQuery(id+"F0.wireOp",EDGE,"E19.filletArc"),sQuery(id+"F0.wireOp",EDGE,"E20.filletArc"),sQuery(id+"F0.wireOp",EDGE,"E25.0"),sQuery(id+"F0.wireOp",EDGE,"E25.1"),sQuery(id+"F0.wireOp",EDGE,"E25.2"),sQuery(id+"F0.wireOp",EDGE,"E25.3"),sQuery(id+"F0.wireOp",EDGE,"E25.4"),sQuery(id+"F0.wireOp",EDGE,"E25.5"),sQuery(id+"F0.wireOp",EDGE,"E25.6"),sQuery(id+"F0.wireOp",EDGE,"E25.7")])],"isStart":false});
            extrude(context, id + "F17", {"entities" : qUnion([Q0]), "endBound" : BoundingType.UP_TO_SURFACE, "endBoundEntityFace" : qUnion([Q1]), "depth" : 25 * mm});
        }
    });
